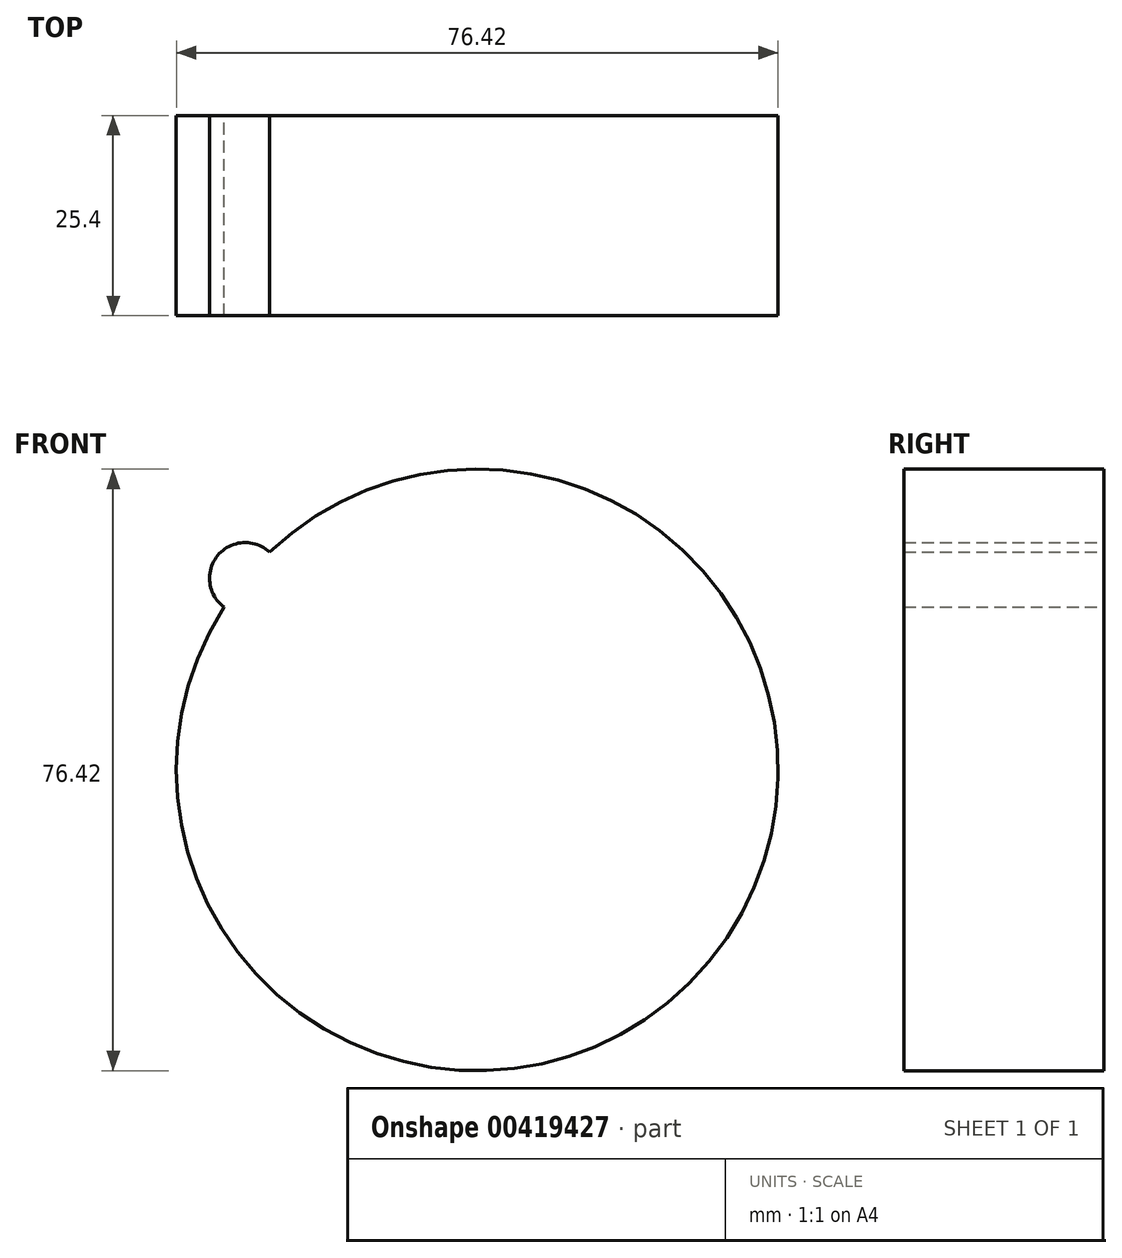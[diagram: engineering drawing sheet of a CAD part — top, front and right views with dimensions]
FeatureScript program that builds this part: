
annotation { "Feature Type Name" : "Feature", "Feature Type Description" : "" }
export const myFeature = defineFeature(function(context is Context, id is Id, definition is map)
    precondition{}
    {
        {
            var Q0;
            Q0=qCreatedBy(makeId("Front.planeOp"),FACE);
            var sketch = newSketch(context, id + "F0", { "sketchPlane" : qUnion([Q0])});
            skCircle(sketch, "E0", {"center": v(0, 0) * mm, "radius": 38.21 * mm});
            skCircle(sketch, "E1", {"center": v(-29.45, 24.34) * mm, "radius": 4.54 * mm});
            skSolve(sketch);
        }
        {
            var Q0;
            Q0 = qSketchRegion(id + "F0", true);
            extrude(context, id + "F1", {"entities" : qUnion([Q0]), "depth" : 25.4 * mm});
        }
    });
